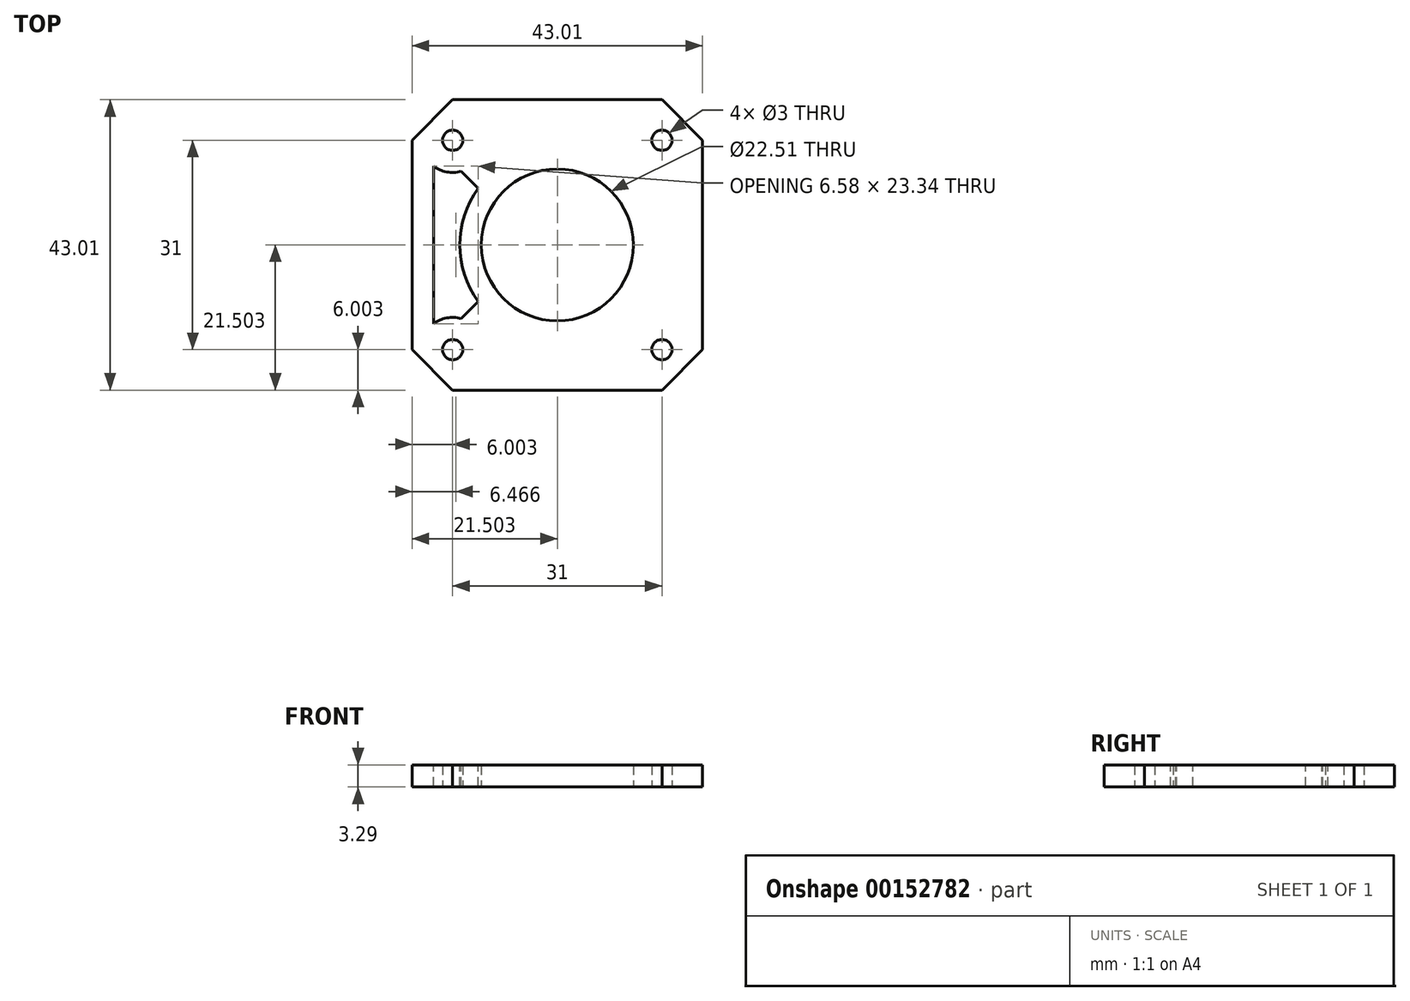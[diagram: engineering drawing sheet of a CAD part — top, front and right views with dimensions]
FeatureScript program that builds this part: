
annotation { "Feature Type Name" : "Feature", "Feature Type Description" : "" }
export const myFeature = defineFeature(function(context is Context, id is Id, definition is map)
    precondition{}
    {
        {
            var Q0;
            Q0=qCreatedBy(makeId("Top.planeOp"),FACE);
            var sketch = newSketch(context, id + "F0", { "sketchPlane" : qUnion([Q0])});
            skLineSegment(sketch, "E0.bottom", {"start": v(0, 0) * mm, "end": v(43, 0) * mm});
            skLineSegment(sketch, "E0.top", {"start": v(0, 43) * mm, "end": v(43, 43) * mm});
            skLineSegment(sketch, "E0.left", {"start": v(0, 0) * mm, "end": v(0, 43) * mm});
            skLineSegment(sketch, "E0.right", {"start": v(43, 0) * mm, "end": v(43, 43) * mm});
            skLineSegment(sketch, "E1", {"start": v(21.5, 43) * mm, "end": v(21.5, 0) * mm, "construction": true});
            skLineSegment(sketch, "E2.bottom", {"start": v(37, 37) * mm, "end": v(6, 37) * mm, "construction": true});
            skLineSegment(sketch, "E2.top", {"start": v(37, 6) * mm, "end": v(6, 6) * mm, "construction": true});
            skLineSegment(sketch, "E2.left", {"start": v(37, 37) * mm, "end": v(37, 6) * mm, "construction": true});
            skLineSegment(sketch, "E2.right", {"start": v(6, 37) * mm, "end": v(6, 6) * mm, "construction": true});
            skPoint(sketch, "E2.middle", {"position": v(21.5, 21.5) * mm});
            skCircle(sketch, "E3", {"center": v(6, 37) * mm, "radius": 1.5 * mm});
            skCircle(sketch, "E4", {"center": v(37, 37) * mm, "radius": 1.5 * mm});
            skCircle(sketch, "E5", {"center": v(21.5, 21.5) * mm, "radius": 11.25 * mm});
            skCircle(sketch, "E6", {"center": v(37, 6) * mm, "radius": 1.5 * mm});
            skCircle(sketch, "E7", {"center": v(6, 6) * mm, "radius": 1.5 * mm});
            skSolve(sketch);
        }
        {
            var Q0;
            Q0=makeQuery(id+"F0.imprint","IMPRINT",FACE,{"disambiguationData":[TD([[makeQuery(id+"F0.imprint","IMPRINT",EDGE,{"derivedFrom":sQuery(id+"F0.wireOp",EDGE,"E0.bottom")}),1.0]])]});
            extrude(context, id + "F1", {"entities" : qUnion([Q0]), "depth" : 3.3 * mm});
        }
        {
            var Q0;
            Q0=makeQuery(id+"F1.opExtrude","SWEPT_EDGE",EDGE,{"disambiguationData":[OSD([sQuery(id+"F0.wireOp",EDGE,"E0.bottom"),sQuery(id+"F0.wireOp",EDGE,"E0.left")])]});
            var Q1;
            Q1=makeQuery(id+"F1.opExtrude","SWEPT_EDGE",EDGE,{"disambiguationData":[OSD([sQuery(id+"F0.wireOp",EDGE,"E0.top"),sQuery(id+"F0.wireOp",EDGE,"E0.left")])]});
            var Q2;
            Q2=makeQuery(id+"F1.opExtrude","SWEPT_EDGE",EDGE,{"disambiguationData":[OSD([sQuery(id+"F0.wireOp",EDGE,"E0.bottom"),sQuery(id+"F0.wireOp",EDGE,"E0.right")])]});
            var Q3;
            Q3=makeQuery(id+"F1.opExtrude","SWEPT_EDGE",EDGE,{"disambiguationData":[OSD([sQuery(id+"F0.wireOp",EDGE,"E0.top"),sQuery(id+"F0.wireOp",EDGE,"E0.right")])]});
            chamfer(context, id + "F2", {"entities" : qUnion([Q0, Q1, Q2, Q3]), "width" : 6 * mm, "tangentPropagation" : true});
        }
        {
            var Q0;
            Q0=makeQuery(id+"F1.opExtrude","CAP_FACE",FACE,{"disambiguationData":[OSD([sQuery(id+"F0.wireOp",EDGE,"E0.bottom"),sQuery(id+"F0.wireOp",EDGE,"E0.top"),sQuery(id+"F0.wireOp",EDGE,"E0.left"),sQuery(id+"F0.wireOp",EDGE,"E0.right"),sQuery(id+"F0.wireOp",EDGE,"E3"),sQuery(id+"F0.wireOp",EDGE,"E4"),sQuery(id+"F0.wireOp",EDGE,"E5"),sQuery(id+"F0.wireOp",EDGE,"E6"),sQuery(id+"F0.wireOp",EDGE,"E7")])],"isStart":false});
            var sketch = newSketch(context, id + "F3", { "sketchPlane" : qUnion([Q0])});
            skLineSegment(sketch, "E8", {"start": v(6, 37) * mm, "end": v(8.92, 34.09) * mm, "construction": true});
            skLineSegment(sketch, "E9", {"start": v(8.92, 34.09) * mm, "end": v(21.5, 21.5) * mm, "construction": true});
            skLineSegment(sketch, "E10", {"start": v(21.5, 21.5) * mm, "end": v(8.92, 8.92) * mm, "construction": true});
            skLineSegment(sketch, "E11", {"start": v(8.92, 8.92) * mm, "end": v(6, 6) * mm, "construction": true});
            skLineSegment(sketch, "E12", {"start": v(0, 21.5) * mm, "end": v(3.18, 21.5) * mm, "construction": true});
            skLineSegment(sketch, "E13", {"start": v(3.17, 33.17) * mm, "end": v(3.18, 9.83) * mm});
            skLineSegment(sketch, "E14", {"start": v(8.92, 34.09) * mm, "end": v(7.24, 32.4) * mm, "construction": true});
            skLineSegment(sketch, "E15", {"start": v(8.92, 8.92) * mm, "end": v(7.24, 10.6) * mm, "construction": true});
            skLineSegment(sketch, "E16", {"start": v(7.24, 32.4) * mm, "end": v(9.76, 29.88) * mm});
            skLineSegment(sketch, "E17", {"start": v(7.24, 10.6) * mm, "end": v(9.76, 13.12) * mm});
            skArc(sketch, "E18", {"start": v(3.17, 33.17) * mm, "mid": v(5.12, 32.32) * mm, "end": v(7.24, 32.4) * mm});
            skArc(sketch, "E19", {"start": v(9.76, 29.88) * mm, "mid": v(7.07, 21.5) * mm, "end": v(9.76, 13.12) * mm});
            skArc(sketch, "E20", {"start": v(7.24, 10.6) * mm, "mid": v(5.12, 10.68) * mm, "end": v(3.17, 9.83) * mm});
            skSolve(sketch);
        }
        {
            var Q0;
            Q0 = qSketchRegion(id + "F3", true);
            var Q1;
            Q1=makeQuery(id+"F1.opExtrude","CAP_FACE",FACE,{"disambiguationData":[OSD([sQuery(id+"F0.wireOp",EDGE,"E0.bottom"),sQuery(id+"F0.wireOp",EDGE,"E0.top"),sQuery(id+"F0.wireOp",EDGE,"E0.left"),sQuery(id+"F0.wireOp",EDGE,"E0.right"),sQuery(id+"F0.wireOp",EDGE,"E3"),sQuery(id+"F0.wireOp",EDGE,"E4"),sQuery(id+"F0.wireOp",EDGE,"E5"),sQuery(id+"F0.wireOp",EDGE,"E6"),sQuery(id+"F0.wireOp",EDGE,"E7")])],"isStart":true});
            extrude(context, id + "F4", {"entities" : qUnion([Q0]), "operationType" : NewBodyOperationType.REMOVE, "endBound" : BoundingType.UP_TO_SURFACE, "oppositeDirection" : true, "endBoundEntityFace" : qUnion([Q1]), "depth" : 25.4 * mm});
        }
    });
